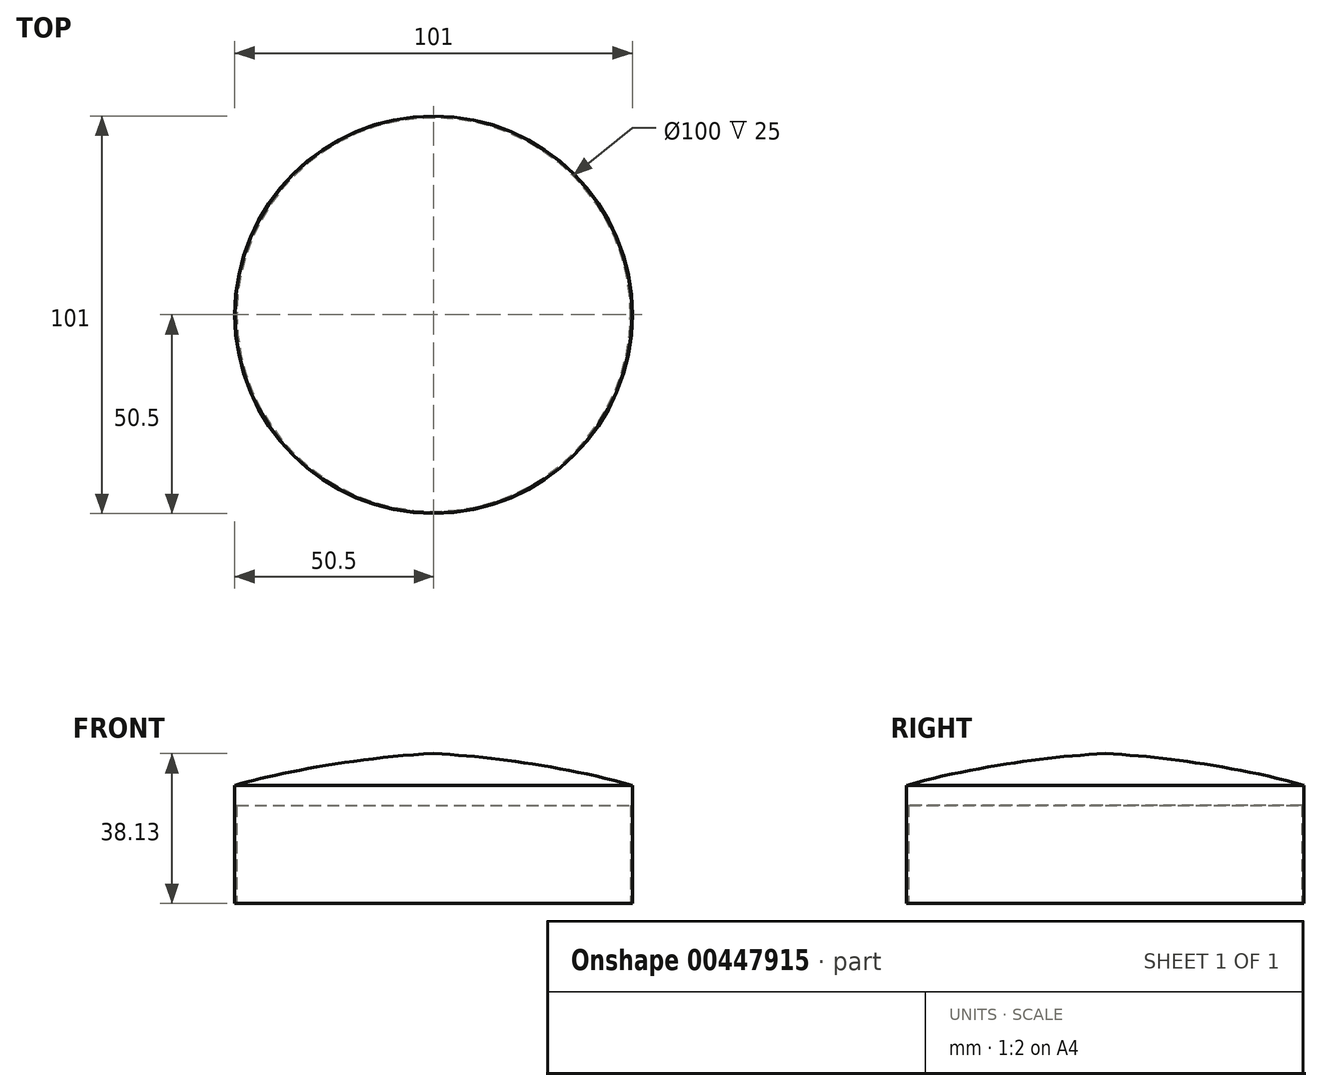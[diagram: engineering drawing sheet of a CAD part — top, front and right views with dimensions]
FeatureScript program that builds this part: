
annotation { "Feature Type Name" : "Feature", "Feature Type Description" : "" }
export const myFeature = defineFeature(function(context is Context, id is Id, definition is map)
    precondition{}
    {
        {
            var Q0;
            Q0=qCreatedBy(makeId("Top.planeOp"),FACE);
            var sketch = newSketch(context, id + "F0", { "sketchPlane" : qUnion([Q0])});
            skCircle(sketch, "E0", {"center": v(0, 0) * mm, "radius": 50.5 * mm});
            skSolve(sketch);
        }
        {
            var Q0;
            Q0=makeQuery(id+"F0.imprint","IMPRINT",FACE,{"disambiguationData":[TD([[makeQuery(id+"F0.imprint","IMPRINT",EDGE,{"derivedFrom":sQuery(id+"F0.wireOp",EDGE,"E0")}),1.0]])]});
            extrude(context, id + "F1", {"entities" : qUnion([Q0]), "depth" : 30 * mm});
        }
        {
            var Q0;
            Q0=makeQuery(id+"F1.opExtrude","CAP_FACE",FACE,{"disambiguationData":[OSD([sQuery(id+"F0.wireOp",EDGE,"E0")])],"isStart":true});
            var sketch = newSketch(context, id + "F2", { "sketchPlane" : qUnion([Q0])});
            skCircle(sketch, "E1", {"center": v(0, 0) * mm, "radius": 50 * mm});
            skSolve(sketch);
        }
        {
            var Q0;
            Q0 = qSketchRegion(id + "F2", true);
            extrude(context, id + "F3", {"entities" : qUnion([Q0]), "operationType" : NewBodyOperationType.REMOVE, "oppositeDirection" : true, "depth" : 25 * mm});
        }
        {
            var Q0;
            Q0=qCreatedBy(makeId("Front.planeOp"),FACE);
            var sketch = newSketch(context, id + "F4", { "sketchPlane" : qUnion([Q0])});
            skLineSegment(sketch, "E2", {"start": v(-50.42, 30.05) * mm, "end": v(0, 30.05) * mm});
            skLineSegment(sketch, "E3", {"start": v(0, 30.05) * mm, "end": v(0, 38.13) * mm});
            skFitSpline(sketch, "E4", {"points": [v(-50.42, 30.05) * mm, v(0, 38.13) * mm], "startDerivative": vector(32.81, 9.57) * mm, "endDerivative": vector(59.4, 3.08) * mm});
            skSolve(sketch);
        }
        {
            var Q0;
            Q0 = qSketchRegion(id + "F4", true);
            var Q1;
            Q1=sQuery(id+"F4.wireOp",EDGE,"E3");
            revolve(context, id + "F5", {"entities" : qUnion([Q0]), "axis" : qUnion([Q1]), "revolveType" : RevolveType.FULL});
        }
    });
